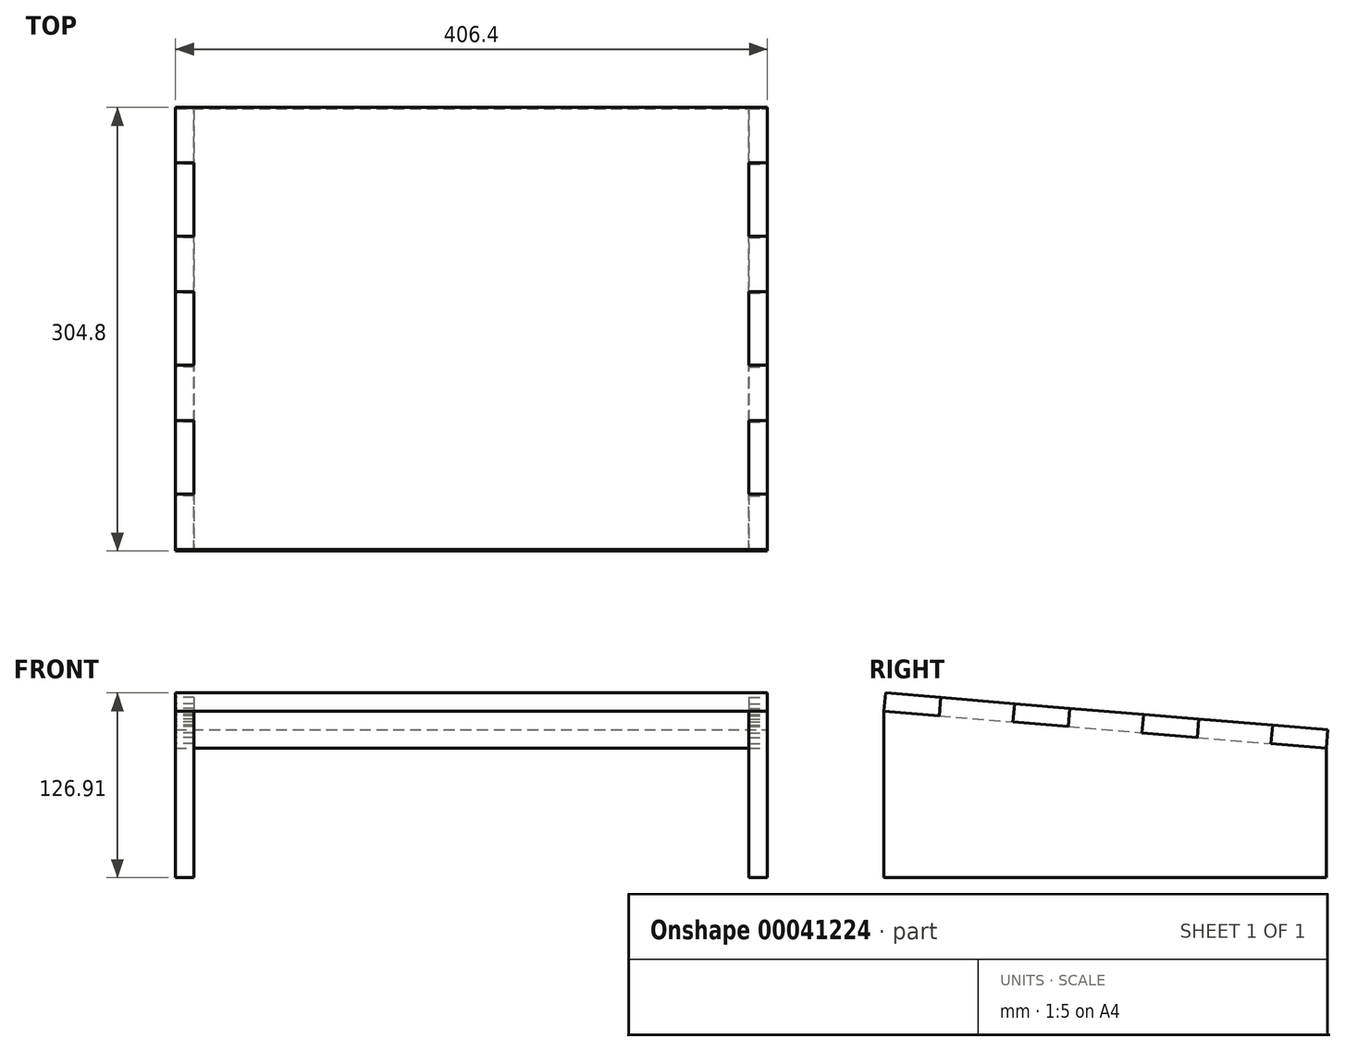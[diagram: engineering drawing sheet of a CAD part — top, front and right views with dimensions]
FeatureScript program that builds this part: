
annotation { "Feature Type Name" : "Feature", "Feature Type Description" : "" }
export const myFeature = defineFeature(function(context is Context, id is Id, definition is map)
    precondition{}
    {
        {
            var Q0;
            Q0=qCreatedBy(makeId("Right.planeOp"),FACE);
            cPlane(context, id + "F0", {"entities" : qUnion([Q0]), "cplaneType" : CPlaneType.OFFSET, "offset" : 203.2 * mm, "width" : 152.4 * mm, "height" : 152.4 * mm});
        }
        {
            var Q0;
            Q0=qCreatedBy(id+"F0.planeOp",FACE);
            var sketch = newSketch(context, id + "F1", { "sketchPlane" : qUnion([Q0])});
            skLineSegment(sketch, "E0", {"start": v(0, 0) * mm, "end": v(0, 114.26) * mm});
            skLineSegment(sketch, "E1", {"start": v(39.03, 123.74) * mm, "end": v(89.65, 119.5) * mm});
            skLineSegment(sketch, "E2", {"start": v(303.74, 88.86) * mm, "end": v(303.74, 0) * mm});
            skLineSegment(sketch, "E3", {"start": v(303.74, 0) * mm, "end": v(0, 0) * mm});
            skLineSegment(sketch, "E4", {"start": v(0, 114.26) * mm, "end": v(37.97, 111.08) * mm});
            skLineSegment(sketch, "E5", {"start": v(89.65, 119.5) * mm, "end": v(88.6, 106.85) * mm});
            skLineSegment(sketch, "E6", {"start": v(127.62, 116.33) * mm, "end": v(126.56, 103.67) * mm});
            skLineSegment(sketch, "E7", {"start": v(178.24, 112.1) * mm, "end": v(177.18, 99.44) * mm});
            skLineSegment(sketch, "E8", {"start": v(216.2, 108.92) * mm, "end": v(215.15, 96.26) * mm});
            skLineSegment(sketch, "E9", {"start": v(266.83, 104.69) * mm, "end": v(265.77, 92.03) * mm});
            skLineSegment(sketch, "E10", {"start": v(37.97, 111.08) * mm, "end": v(39.03, 123.74) * mm});
            skLineSegment(sketch, "E11.trimOffspring", {"start": v(127.62, 116.33) * mm, "end": v(178.24, 112.1) * mm});
            skLineSegment(sketch, "E12.trimOffspring", {"start": v(216.2, 108.92) * mm, "end": v(266.83, 104.69) * mm});
            skLineSegment(sketch, "E13.trimOffspring", {"start": v(177.18, 99.44) * mm, "end": v(215.15, 96.26) * mm});
            skLineSegment(sketch, "E14.trimOffspring", {"start": v(88.6, 106.85) * mm, "end": v(126.56, 103.67) * mm});
            skLineSegment(sketch, "E15.trimOffspring", {"start": v(265.77, 92.03) * mm, "end": v(303.74, 88.86) * mm});
            skSolve(sketch);
        }
        {
            var Q0;
            Q0 = qSketchRegion(id + "F1", true);
            extrude(context, id + "F2", {"entities" : qUnion([Q0]), "oppositeDirection" : true, "depth" : 12.7 * mm});
        }
        {
            var Q0;
            Q0=makeQuery(id+"F2.opExtrude","SWEPT_BODY",BODY,{"disambiguationData":[OSD([sQuery(id+"F1.wireOp",EDGE,"E0"),sQuery(id+"F1.wireOp",EDGE,"E1"),sQuery(id+"F1.wireOp",EDGE,"E2"),sQuery(id+"F1.wireOp",EDGE,"E3"),sQuery(id+"F1.wireOp",EDGE,"E4"),sQuery(id+"F1.wireOp",EDGE,"E5"),sQuery(id+"F1.wireOp",EDGE,"E6"),sQuery(id+"F1.wireOp",EDGE,"E7"),sQuery(id+"F1.wireOp",EDGE,"E8"),sQuery(id+"F1.wireOp",EDGE,"E9"),sQuery(id+"F1.wireOp",EDGE,"E10"),sQuery(id+"F1.wireOp",EDGE,"E11.trimOffspring"),sQuery(id+"F1.wireOp",EDGE,"E12.trimOffspring"),sQuery(id+"F1.wireOp",EDGE,"E13.trimOffspring"),sQuery(id+"F1.wireOp",EDGE,"E14.trimOffspring"),sQuery(id+"F1.wireOp",EDGE,"E15.trimOffspring")])]});
            var Q1;
            Q1=qCreatedBy(makeId("Right.planeOp"),FACE);
            mirror(context, id + "F3", {"entities" : qUnion([Q0]), "mirrorPlane" : qUnion([Q1])});
        }
        {
            var Q0;
            Q0=makeQuery(id+"F2.opExtrude","SWEPT_FACE",FACE,{"disambiguationData":[OSD([sQuery(id+"F1.wireOp",EDGE,"E15.trimOffspring")])]});
            var sketch = newSketch(context, id + "F4", { "sketchPlane" : qUnion([Q0])});
            skLineSegment(sketch, "E16.0", {"start": v(190.5, 295.28) * mm, "end": v(203.2, 295.28) * mm});
            skLineSegment(sketch, "E17.0", {"start": v(203.2, 257.18) * mm, "end": v(203.2, 295.28) * mm});
            skLineSegment(sketch, "E18.0", {"start": v(190.5, 257.18) * mm, "end": v(203.2, 257.18) * mm});
            skLineSegment(sketch, "E19.0", {"start": v(190.5, 206.38) * mm, "end": v(190.5, 257.18) * mm});
            skLineSegment(sketch, "E20.0", {"start": v(190.5, 206.38) * mm, "end": v(203.2, 206.38) * mm});
            skLineSegment(sketch, "E21.0", {"start": v(203.2, 168.28) * mm, "end": v(203.2, 206.38) * mm});
            skLineSegment(sketch, "E22.0", {"start": v(190.5, 168.28) * mm, "end": v(203.2, 168.28) * mm});
            skLineSegment(sketch, "E23.0", {"start": v(190.5, 117.48) * mm, "end": v(190.5, 168.28) * mm});
            skLineSegment(sketch, "E24.0", {"start": v(190.5, 117.48) * mm, "end": v(203.2, 117.48) * mm});
            skLineSegment(sketch, "E25.0", {"start": v(203.2, 79.38) * mm, "end": v(203.2, 117.48) * mm});
            skLineSegment(sketch, "E26.0", {"start": v(190.5, 79.38) * mm, "end": v(203.2, 79.38) * mm});
            skLineSegment(sketch, "E27.0", {"start": v(190.5, 28.58) * mm, "end": v(190.5, 79.38) * mm});
            skLineSegment(sketch, "E28.0", {"start": v(190.5, 28.58) * mm, "end": v(203.2, 28.58) * mm});
            skLineSegment(sketch, "E29.0", {"start": v(203.2, -9.52) * mm, "end": v(203.2, 28.58) * mm});
            skLineSegment(sketch, "E30.0", {"start": v(-203.2, -9.52) * mm, "end": v(-203.2, 28.58) * mm});
            skLineSegment(sketch, "E31.0", {"start": v(-190.5, 28.58) * mm, "end": v(-203.2, 28.58) * mm});
            skLineSegment(sketch, "E32.0", {"start": v(-190.5, 28.58) * mm, "end": v(-190.5, 79.38) * mm});
            skLineSegment(sketch, "E33.0", {"start": v(-190.5, 79.38) * mm, "end": v(-203.2, 79.38) * mm});
            skLineSegment(sketch, "E34.0", {"start": v(-203.2, 79.38) * mm, "end": v(-203.2, 117.48) * mm});
            skLineSegment(sketch, "E35.0", {"start": v(-190.5, 117.48) * mm, "end": v(-203.2, 117.48) * mm});
            skLineSegment(sketch, "E36.0", {"start": v(-190.5, 117.48) * mm, "end": v(-190.5, 168.28) * mm});
            skLineSegment(sketch, "E37.0", {"start": v(-190.5, 168.28) * mm, "end": v(-203.2, 168.28) * mm});
            skLineSegment(sketch, "E38.0", {"start": v(-203.2, 168.28) * mm, "end": v(-203.2, 206.38) * mm});
            skLineSegment(sketch, "E39.0", {"start": v(-190.5, 206.38) * mm, "end": v(-203.2, 206.38) * mm});
            skLineSegment(sketch, "E40.0", {"start": v(-190.5, 206.38) * mm, "end": v(-190.5, 257.18) * mm});
            skLineSegment(sketch, "E41.0", {"start": v(-190.5, 257.18) * mm, "end": v(-203.2, 257.18) * mm});
            skLineSegment(sketch, "E42.0", {"start": v(-203.2, 257.18) * mm, "end": v(-203.2, 295.28) * mm});
            skPoint(sketch, "E43.0.start.orphan", {"position": v(-190.5, 295.28) * mm});
            skLineSegment(sketch, "E44", {"start": v(-203.2, 295.28) * mm, "end": v(203.2, 295.28) * mm});
            skLineSegment(sketch, "E45", {"start": v(203.2, -9.52) * mm, "end": v(-203.2, -9.52) * mm});
            skSolve(sketch);
        }
        {
            var Q0;
            Q0 = qSketchRegion(id + "F4", true);
            extrude(context, id + "F5", {"entities" : qUnion([Q0]), "depth" : 12.7 * mm});
        }
    });
